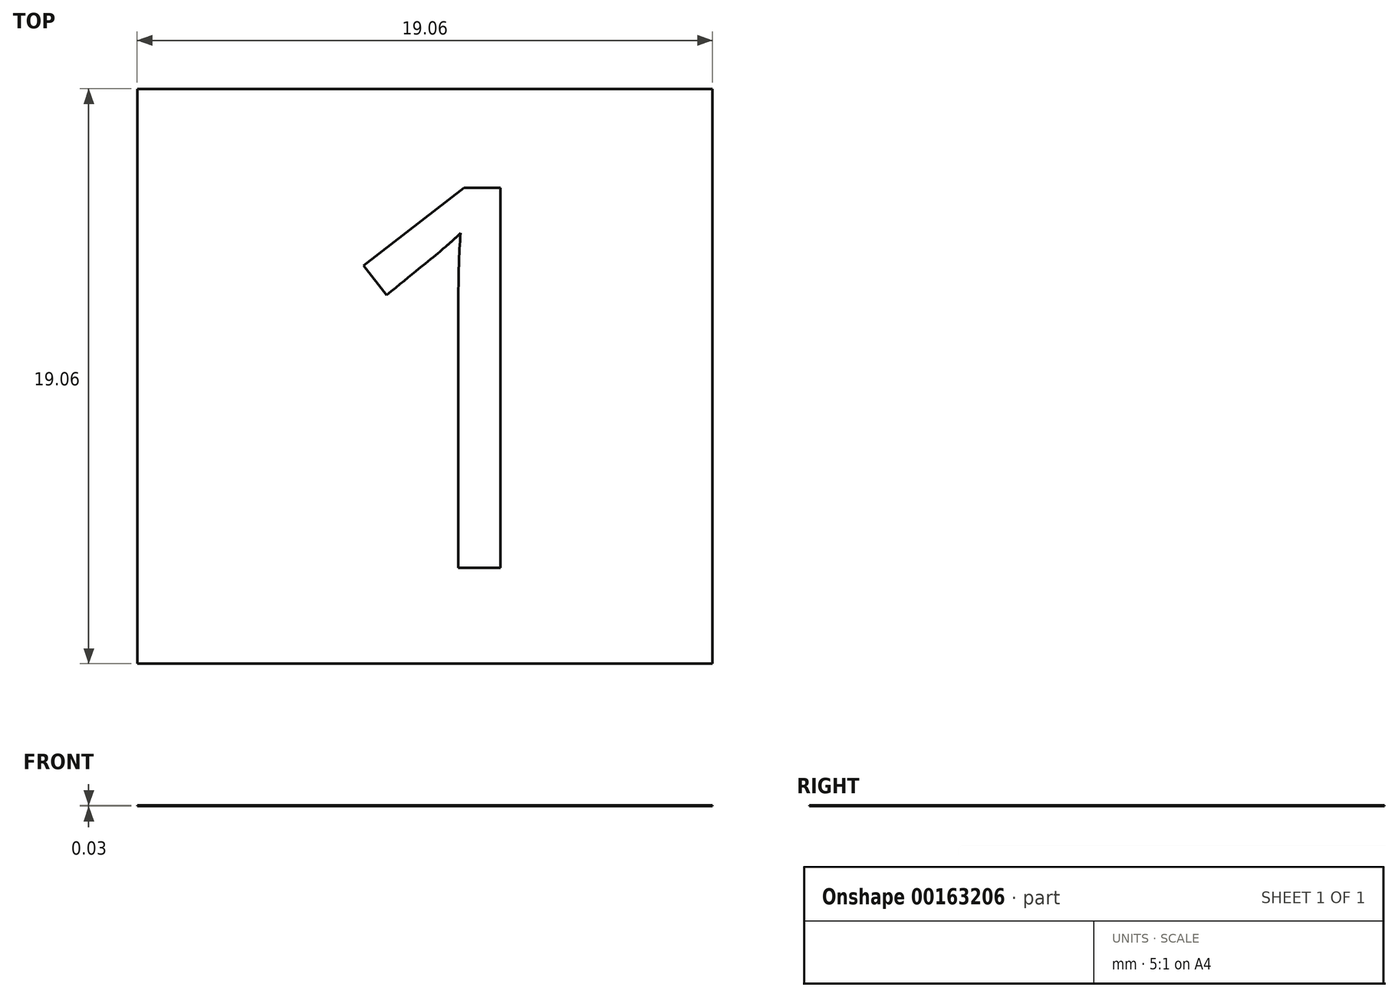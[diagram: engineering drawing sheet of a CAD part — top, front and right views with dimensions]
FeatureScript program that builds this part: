
annotation { "Feature Type Name" : "Feature", "Feature Type Description" : "" }
export const myFeature = defineFeature(function(context is Context, id is Id, definition is map)
    precondition{}
    {
        {
            var Q0;
            Q0=qCreatedBy(makeId("Top.planeOp"),FACE);
            var sketch = newSketch(context, id + "F0", { "sketchPlane" : qUnion([Q0])});
            skLineSegment(sketch, "E0.bottom", {"start": v(9.53, 9.52) * mm, "end": v(-9.52, 9.52) * mm});
            skLineSegment(sketch, "E0.top", {"start": v(9.53, -9.53) * mm, "end": v(-9.53, -9.53) * mm});
            skLineSegment(sketch, "E0.left", {"start": v(9.53, 9.52) * mm, "end": v(9.53, -9.53) * mm});
            skLineSegment(sketch, "E0.right", {"start": v(-9.53, 9.52) * mm, "end": v(-9.53, -9.53) * mm});
            skPoint(sketch, "E0.middle", {"position": v(0, 0) * mm});
            skSolve(sketch);
        }
        {
            var Q0;
            Q0 = qSketchRegion(id + "F0", true);
            extrude(context, id + "F1", {"entities" : qUnion([Q0]), "depth" : 3 / 101.6 * mm});
        }
        {
            var Q0;
            Q0=qCreatedBy(makeId("Top.planeOp"),FACE);
            cPlane(context, id + "F2", {"entities" : qUnion([Q0]), "cplaneType" : CPlaneType.OFFSET, "offset" : 19.05 * mm, "width" : 152.4 * mm, "height" : 152.4 * mm});
        }
        {
            var Q0;
            Q0=qCreatedBy(id+"F2.planeOp",FACE);
            var sketch = newSketch(context, id + "F3", { "sketchPlane" : qUnion([Q0])});
            skText(sketch, "E1", { "text": "1", "fontName": "OpenSans-Regular.ttf"});
            skLineSegment(sketch, "E2", {"start": v(-3.65, 6.35) * mm, "end": v(3.65, -6.35) * mm, "construction": true});
            skLineSegment(sketch, "E3", {"start": v(3.65, 6.35) * mm, "end": v(-3.65, -6.35) * mm, "construction": true});
            skPoint(sketch, "E4", {"position": v(0, 0) * mm});
            const initialGuessF3  = {"E1": [-0.00365, -0.00635, 1, 0, 0.0127]};
            skSetInitialGuess(sketch, initialGuessF3);
            skSolve(sketch);
        }
        {
            var Q0;
            Q0 = qSketchRegion(id + "F3", true);
            extrude(context, id + "F4", {"entities" : qUnion([Q0]), "operationType" : NewBodyOperationType.REMOVE, "endBound" : BoundingType.THROUGH_ALL, "oppositeDirection" : true, "depth" : 1 / 406.4 * mm});
        }
    });
